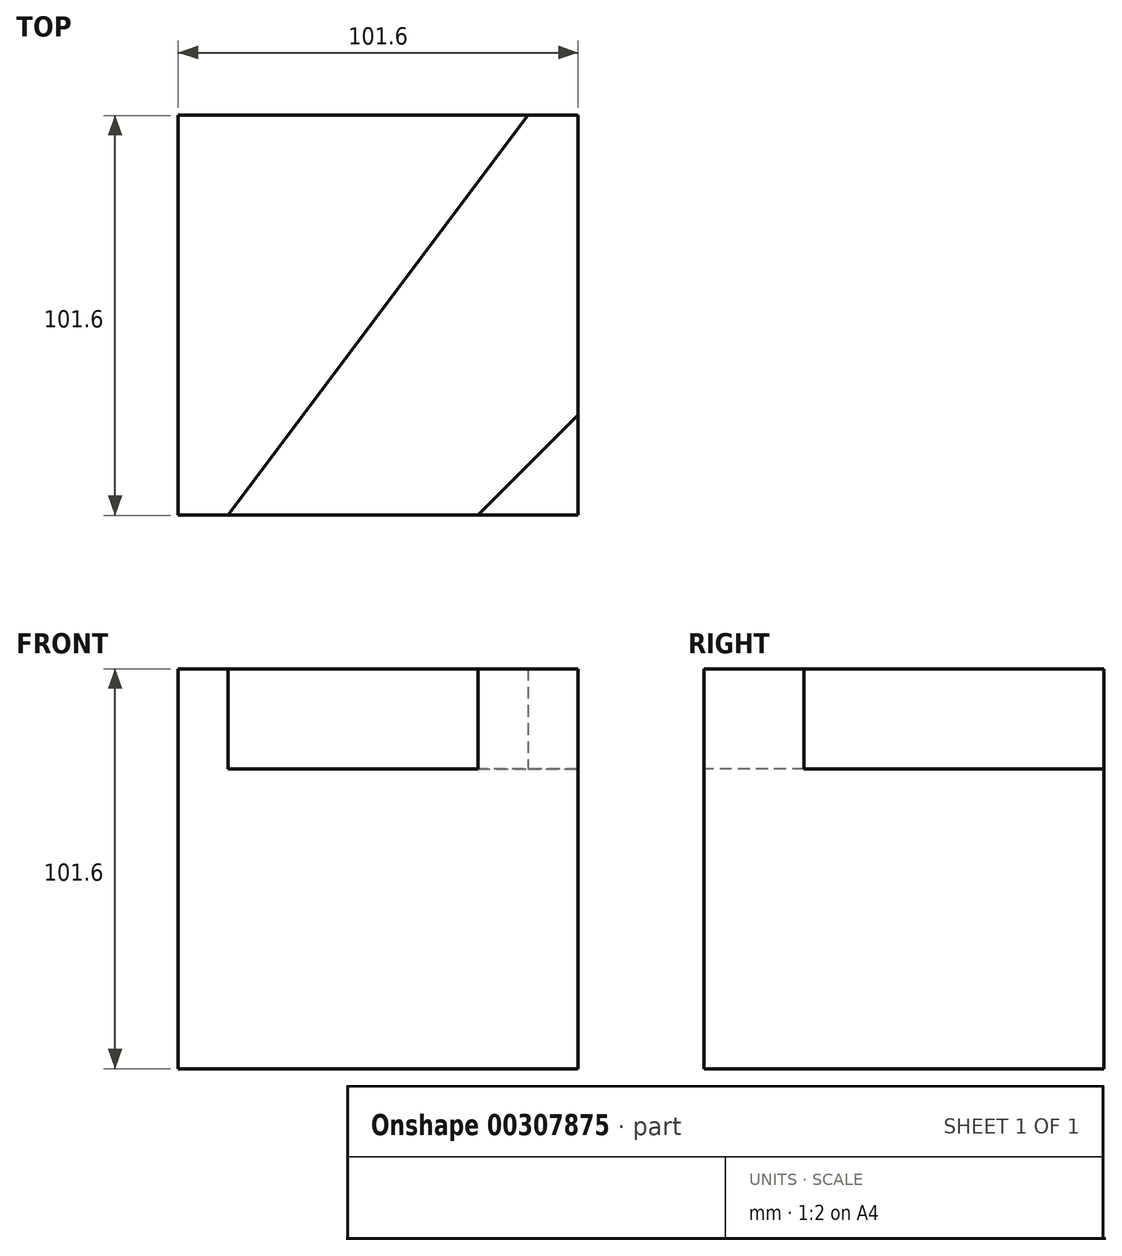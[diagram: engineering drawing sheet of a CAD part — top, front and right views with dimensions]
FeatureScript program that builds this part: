
annotation { "Feature Type Name" : "Feature", "Feature Type Description" : "" }
export const myFeature = defineFeature(function(context is Context, id is Id, definition is map)
    precondition{}
    {
        {
            var Q0;
            Q0=qCreatedBy(makeId("Top.planeOp"),FACE);
            var sketch = newSketch(context, id + "F0", { "sketchPlane" : qUnion([Q0])});
            skLineSegment(sketch, "E0.bottom", {"start": v(-48.87, 47.73) * mm, "end": v(52.73, 47.73) * mm});
            skLineSegment(sketch, "E0.top", {"start": v(-48.87, -53.87) * mm, "end": v(52.73, -53.87) * mm});
            skLineSegment(sketch, "E0.left", {"start": v(-48.87, 47.73) * mm, "end": v(-48.87, -53.87) * mm});
            skLineSegment(sketch, "E0.right", {"start": v(52.73, 47.73) * mm, "end": v(52.73, -53.87) * mm});
            skSolve(sketch);
        }
        {
            var Q0;
            Q0=makeQuery(id+"F0.imprint","IMPRINT",FACE,{"disambiguationData":[TD([[makeQuery(id+"F0.imprint","IMPRINT",EDGE,{"derivedFrom":sQuery(id+"F0.wireOp",EDGE,"E0.bottom")}),-1.0]])]});
            extrude(context, id + "F1", {"entities" : qUnion([Q0]), "depth" : 76.2 * mm});
        }
        {
            var Q0;
            Q0=makeQuery(id+"F1.opExtrude","CAP_FACE",FACE,{"disambiguationData":[OSD([sQuery(id+"F0.wireOp",EDGE,"E0.bottom"),sQuery(id+"F0.wireOp",EDGE,"E0.top"),sQuery(id+"F0.wireOp",EDGE,"E0.left"),sQuery(id+"F0.wireOp",EDGE,"E0.right")])],"isStart":false});
            var sketch = newSketch(context, id + "F2", { "sketchPlane" : qUnion([Q0])});
            skLineSegment(sketch, "E1", {"start": v(-48.87, -53.87) * mm, "end": v(-36.17, -53.87) * mm});
            skLineSegment(sketch, "E2", {"start": v(-36.17, -53.87) * mm, "end": v(40.03, 47.73) * mm});
            skLineSegment(sketch, "E3", {"start": v(40.03, 47.73) * mm, "end": v(-48.87, 47.73) * mm});
            skLineSegment(sketch, "E4", {"start": v(-48.87, 47.73) * mm, "end": v(-48.87, -53.87) * mm});
            skLineSegment(sketch, "E5", {"start": v(27.33, -53.87) * mm, "end": v(52.73, -53.87) * mm});
            skLineSegment(sketch, "E6", {"start": v(52.73, -53.87) * mm, "end": v(52.73, -28.47) * mm});
            skLineSegment(sketch, "E7", {"start": v(52.73, -28.47) * mm, "end": v(27.33, -53.87) * mm});
            skSolve(sketch);
        }
        {
            var Q0;
            Q0=makeQuery(id+"F2.imprint","IMPRINT",FACE,{"disambiguationData":[TD([[makeQuery(id+"F2.imprint","IMPRINT",EDGE,{"derivedFrom":sQuery(id+"F2.wireOp",EDGE,"E1")}),1.0]])]});
            extrude(context, id + "F3", {"entities" : qUnion([Q0]), "operationType" : NewBodyOperationType.ADD, "depth" : 25.4 * mm});
        }
        {
            var Q0;
            Q0=makeQuery(id+"F1.opExtrude","CAP_FACE",FACE,{"disambiguationData":[OSD([sQuery(id+"F0.wireOp",EDGE,"E0.bottom"),sQuery(id+"F0.wireOp",EDGE,"E0.top"),sQuery(id+"F0.wireOp",EDGE,"E0.left"),sQuery(id+"F0.wireOp",EDGE,"E0.right")])],"isStart":false});
            var sketch = newSketch(context, id + "F4", { "sketchPlane" : qUnion([Q0])});
            skLineSegment(sketch, "E8", {"start": v(27.33, -53.87) * mm, "end": v(52.73, -53.87) * mm});
            skLineSegment(sketch, "E9", {"start": v(52.73, -53.87) * mm, "end": v(52.73, -28.47) * mm});
            skLineSegment(sketch, "E10", {"start": v(52.73, -28.47) * mm, "end": v(27.33, -53.87) * mm});
            skSolve(sketch);
        }
        {
            var Q0;
            Q0=makeQuery(id+"F4.imprint","IMPRINT",FACE,{"disambiguationData":[TD([[makeQuery(id+"F4.imprint","IMPRINT",EDGE,{"derivedFrom":sQuery(id+"F4.wireOp",EDGE,"E8")}),1.0]])]});
            extrude(context, id + "F5", {"entities" : qUnion([Q0]), "operationType" : NewBodyOperationType.ADD, "depth" : 25.4 * mm});
        }
    });
